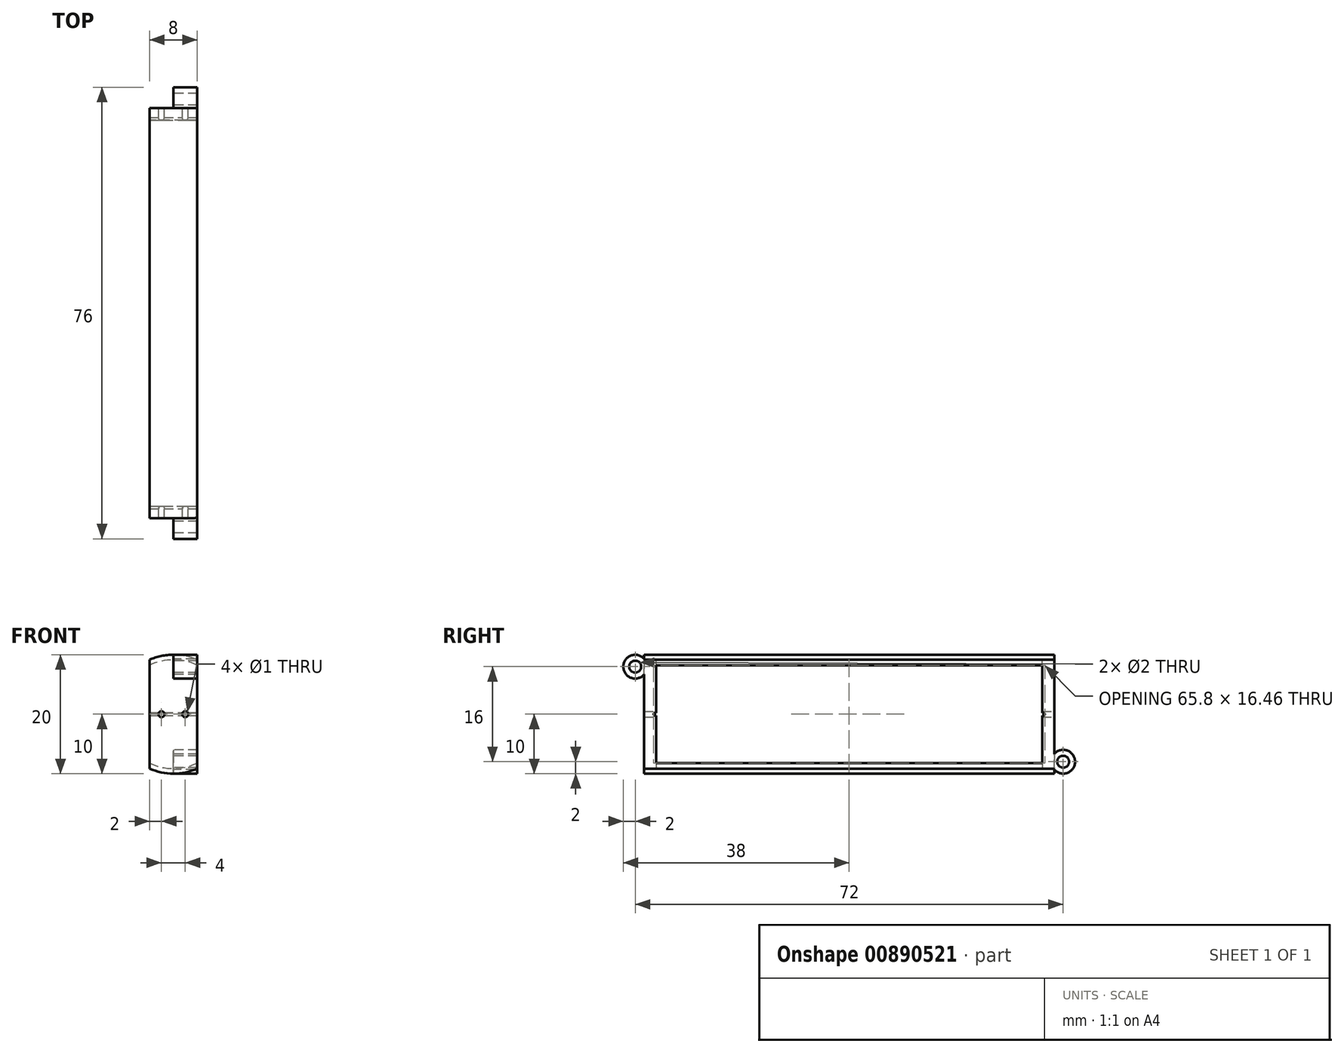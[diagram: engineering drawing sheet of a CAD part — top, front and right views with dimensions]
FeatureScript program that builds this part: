
annotation { "Feature Type Name" : "Feature", "Feature Type Description" : "" }
export const myFeature = defineFeature(function(context is Context, id is Id, definition is map)
    precondition{}
    {
        {
            var Q0;
            Q0=qCreatedBy(makeId("Front.planeOp"),FACE);
            var sketch = newSketch(context, id + "F0", { "sketchPlane" : qUnion([Q0])});
            skCircle(sketch, "E0", {"center": v(0, 0) * mm, "radius": 9.15 * mm});
            skCircle(sketch, "E1", {"center": v(0, 0) * mm, "radius": 10 * mm});
            skSolve(sketch);
        }
        {
            var Q0;
            Q0=makeQuery(id+"F0.imprint","IMPRINT",FACE,{"disambiguationData":[TD([[makeQuery(id+"F0.imprint","IMPRINT",EDGE,{"derivedFrom":sQuery(id+"F0.wireOp",EDGE,"E0")}),-1.0]])]});
            extrude(context, id + "F1", {"entities" : qUnion([Q0]), "depth" : 65 * mm, "offsetDistance" : 25 * mm, "symmetric" : true});
        }
        {
            var Q0;
            Q0=makeQuery(id+"F1.opExtrude","CAP_FACE",FACE,{"disambiguationData":[OSD([sQuery(id+"F0.wireOp",EDGE,"E0"),sQuery(id+"F0.wireOp",EDGE,"E1")])],"isStart":false});
            var sketch = newSketch(context, id + "F2", { "sketchPlane" : qUnion([Q0])});
            skSolve(sketch);
        }
        {
            var Q0;
            Q0=makeQuery(id+"F2.imprint","IMPRINT",FACE,{"disambiguationData":[TD([[makeQuery(id+"F2.imprint","IMPRINT",EDGE,{"derivedFrom":makeQuery(id+"F1.opExtrude","CAP_EDGE",EDGE,{"disambiguationData":[OSD([sQuery(id+"F0.wireOp",EDGE,"E0")])],"isStart":false})}),-1.0]])]});
            var sketch = newSketch(context, id + "F3", { "sketchPlane" : qUnion([Q0])});
            skCircle(sketch, "E2", {"center": v(0, 0) * mm, "radius": 10 * mm});
            skSolve(sketch);
        }
        {
            var Q0;
            Q0 = qSketchRegion(id + "F3", true);
            extrude(context, id + "F4", {"entities" : qUnion([Q0]), "operationType" : NewBodyOperationType.ADD, "depth" : 2 * mm, "offsetDistance" : 25 * mm});
        }
        {
            var Q0;
            Q0=makeQuery(id+"F1.opExtrude","CAP_FACE",FACE,{"disambiguationData":[OSD([sQuery(id+"F0.wireOp",EDGE,"E0"),sQuery(id+"F0.wireOp",EDGE,"E1")])],"isStart":true});
            var sketch = newSketch(context, id + "F5", { "sketchPlane" : qUnion([Q0])});
            skCircle(sketch, "E3", {"center": v(0, 0) * mm, "radius": 10 * mm});
            skSolve(sketch);
        }
        {
            var Q0;
            Q0=makeQuery(id+"F5.imprint","IMPRINT",FACE,{"disambiguationData":[TD([[makeQuery(id+"F5.imprint","IMPRINT",EDGE,{"derivedFrom":makeQuery(id+"F1.opExtrude","CAP_EDGE",EDGE,{"disambiguationData":[OSD([sQuery(id+"F0.wireOp",EDGE,"E0")])],"isStart":true})}),1.0]])]});
            var sketch = newSketch(context, id + "F6", { "sketchPlane" : qUnion([Q0])});
            skCircle(sketch, "E4", {"center": v(0, 0) * mm, "radius": 10 * mm});
            skSolve(sketch);
        }
        {
            var Q0;
            Q0 = qSketchRegion(id + "F6", true);
            extrude(context, id + "F7", {"entities" : qUnion([Q0]), "operationType" : NewBodyOperationType.ADD, "depth" : 2 * mm, "offsetDistance" : 25 * mm});
        }
        {
            var Q0;
            Q0=qCreatedBy(makeId("Top.planeOp"),FACE);
            cPlane(context, id + "F8", {"entities" : qUnion([Q0]), "cplaneType" : CPlaneType.OFFSET, "offset" : 11 * mm, "width" : 150 * mm, "height" : 150 * mm});
        }
        {
            var Q0;
            Q0=qCreatedBy(id+"F8.planeOp",FACE);
            var sketch = newSketch(context, id + "F9", { "sketchPlane" : qUnion([Q0])});
            skLineSegment(sketch, "E5.bottom", {"start": v(-4, 37.5) * mm, "end": v(-24.54, 37.5) * mm});
            skLineSegment(sketch, "E5.top", {"start": v(-4, -37.5) * mm, "end": v(-24.54, -37.5) * mm});
            skLineSegment(sketch, "E5.left", {"start": v(-4, 37.5) * mm, "end": v(-4, -37.5) * mm});
            skLineSegment(sketch, "E5.right", {"start": v(-24.54, 37.5) * mm, "end": v(-24.54, -37.5) * mm});
            skPoint(sketch, "E5.middle", {"position": v(-14.27, 0) * mm});
            skLineSegment(sketch, "E6.bottom", {"start": v(4, 37.5) * mm, "end": v(23.67, 37.5) * mm});
            skLineSegment(sketch, "E6.top", {"start": v(4, -37.5) * mm, "end": v(23.67, -37.5) * mm});
            skLineSegment(sketch, "E6.left", {"start": v(4, 37.5) * mm, "end": v(4, -37.5) * mm});
            skLineSegment(sketch, "E6.right", {"start": v(23.67, 37.5) * mm, "end": v(23.67, -37.5) * mm});
            skPoint(sketch, "E6.middle", {"position": v(13.84, 0) * mm});
            skSolve(sketch);
        }
        {
            var Q0;
            Q0=makeQuery(id+"F9.imprint","IMPRINT",FACE,{"disambiguationData":[TD([[makeQuery(id+"F9.imprint","IMPRINT",EDGE,{"derivedFrom":sQuery(id+"F9.wireOp",EDGE,"E5.bottom")}),1.0]])]});
            var Q1;
            Q1=makeQuery(id+"F9.imprint","IMPRINT",FACE,{"disambiguationData":[TD([[makeQuery(id+"F9.imprint","IMPRINT",EDGE,{"derivedFrom":sQuery(id+"F9.wireOp",EDGE,"E6.bottom")}),-1.0]])]});
            extrude(context, id + "F10", {"entities" : qUnion([Q0, Q1]), "operationType" : NewBodyOperationType.REMOVE, "oppositeDirection" : true, "depth" : 25 * mm, "offsetDistance" : 25 * mm});
        }
        {
            var Q0;
            Q0=makeQuery(id+"F10.boolean.opBoolean","COPY",FACE,{"derivedFrom":makeQuery(id+"F10.opExtrude","SWEPT_FACE",FACE,{"disambiguationData":[OSD([sQuery(id+"F9.wireOp",EDGE,"E6.left")])]})});
            var sketch = newSketch(context, id + "F11", { "sketchPlane" : qUnion([Q0])});
            skCircle(sketch, "E7", {"center": v(-32.65, 0) * mm, "radius": 0.25 * mm});
            skCircle(sketch, "E8", {"center": v(32.65, 0) * mm, "radius": 0.25 * mm});
            skSolve(sketch);
        }
        {
            var Q0;
            {var subQ0=sQuery(id+"F11.wireOp",EDGE,"E7");var subQ1=makeQuery(id+"F10.boolean.opBoolean","INTERSECT",EDGE,{"derivedFrom":[makeQuery(id+"F4.opExtrude","CAP_FACE",FACE,{"disambiguationData":[OSD([sQuery(id+"F3.wireOp",EDGE,"E2")])],"isStart":true}),makeQuery(id+"F10.opExtrude","SWEPT_FACE",FACE,{"disambiguationData":[OSD([sQuery(id+"F9.wireOp",EDGE,"E6.left")])]})]});var subQ2=makeQuery(id+"F11.imprint","INTERSECT",VERTEX,{"disambiguationData":[OD(0.0)],"derivedFrom":[subQ1,subQ0]});Q0=makeQuery(id+"F11.imprint","IMPRINT",FACE,{"disambiguationData":[TD([[makeQuery(id+"F11.imprint","IMPRINT",EDGE,{"disambiguationData":[TD([[subQ2,1.0]])],"derivedFrom":subQ0}),1.0]])]});}
            var Q1;
            {var subQ0=sQuery(id+"F11.wireOp",EDGE,"E8");var subQ1=makeQuery(id+"F10.boolean.opBoolean","INTERSECT",EDGE,{"derivedFrom":[makeQuery(id+"F7.opExtrude","CAP_FACE",FACE,{"disambiguationData":[OSD([sQuery(id+"F6.wireOp",EDGE,"E4")])],"isStart":true}),makeQuery(id+"F10.opExtrude","SWEPT_FACE",FACE,{"disambiguationData":[OSD([sQuery(id+"F9.wireOp",EDGE,"E6.left")])]})]});var subQ2=makeQuery(id+"F11.imprint","INTERSECT",VERTEX,{"disambiguationData":[OD(0.0)],"derivedFrom":[subQ1,subQ0]});Q1=makeQuery(id+"F11.imprint","IMPRINT",FACE,{"disambiguationData":[TD([[makeQuery(id+"F11.imprint","IMPRINT",EDGE,{"disambiguationData":[TD([[subQ2,-1.0]])],"derivedFrom":subQ0}),1.0]])]});}
            extrude(context, id + "F12", {"entities" : qUnion([Q0, Q1]), "operationType" : NewBodyOperationType.REMOVE, "oppositeDirection" : true, "depth" : 25 * mm, "offsetDistance" : 25 * mm});
        }
        {
            var Q0;
            Q0=makeQuery(id+"F7.opExtrude","CAP_FACE",FACE,{"disambiguationData":[OSD([sQuery(id+"F6.wireOp",EDGE,"E4")])],"isStart":false});
            var sketch = newSketch(context, id + "F13", { "sketchPlane" : qUnion([Q0])});
            skCircle(sketch, "E9", {"center": v(-2, 0) * mm, "radius": 0.5 * mm});
            skCircle(sketch, "E10", {"center": v(2, 0) * mm, "radius": 0.5 * mm});
            skSolve(sketch);
        }
        {
            var Q0;
            Q0 = qSketchRegion(id + "F13", true);
            extrude(context, id + "F14", {"entities" : qUnion([Q0]), "operationType" : NewBodyOperationType.REMOVE, "oppositeDirection" : true, "depth" : 80 * mm, "offsetDistance" : 25 * mm});
        }
        {
            var Q0;
            Q0=qCreatedBy(makeId("Right.planeOp"),FACE);
            var sketch = newSketch(context, id + "F15", { "sketchPlane" : qUnion([Q0])});
            skCircle(sketch, "E11", {"center": v(36, -8) * mm, "radius": 2 * mm});
            skCircle(sketch, "E12", {"center": v(36, -8) * mm, "radius": 1 * mm});
            skSolve(sketch);
        }
        {
            var Q0;
            Q0=makeQuery(id+"F15.imprint","IMPRINT",FACE,{"disambiguationData":[TD([[makeQuery(id+"F15.imprint","IMPRINT",EDGE,{"derivedFrom":sQuery(id+"F15.wireOp",EDGE,"E11")}),1.0]])]});
            extrude(context, id + "F16", {"entities" : qUnion([Q0]), "operationType" : NewBodyOperationType.ADD, "depth" : 4 * mm, "offsetDistance" : 25 * mm});
        }
        {
            var Q0;
            Q0=qCreatedBy(makeId("Right.planeOp"),FACE);
            var sketch = newSketch(context, id + "F17", { "sketchPlane" : qUnion([Q0])});
            skCircle(sketch, "E13", {"center": v(-36, 8) * mm, "radius": 1 * mm});
            skPoint(sketch, "E13.centerSnap0", {"position": v(-23.5, 0) * mm});
            skCircle(sketch, "E14", {"center": v(-36, 8) * mm, "radius": 2 * mm});
            skSolve(sketch);
        }
        {
            var Q0;
            Q0=makeQuery(id+"F17.imprint","IMPRINT",FACE,{"disambiguationData":[TD([[makeQuery(id+"F17.imprint","IMPRINT",EDGE,{"derivedFrom":sQuery(id+"F17.wireOp",EDGE,"E13")}),-1.0]])]});
            extrude(context, id + "F18", {"entities" : qUnion([Q0]), "operationType" : NewBodyOperationType.ADD, "depth" : 4 * mm, "offsetDistance" : 25 * mm});
        }
    });
